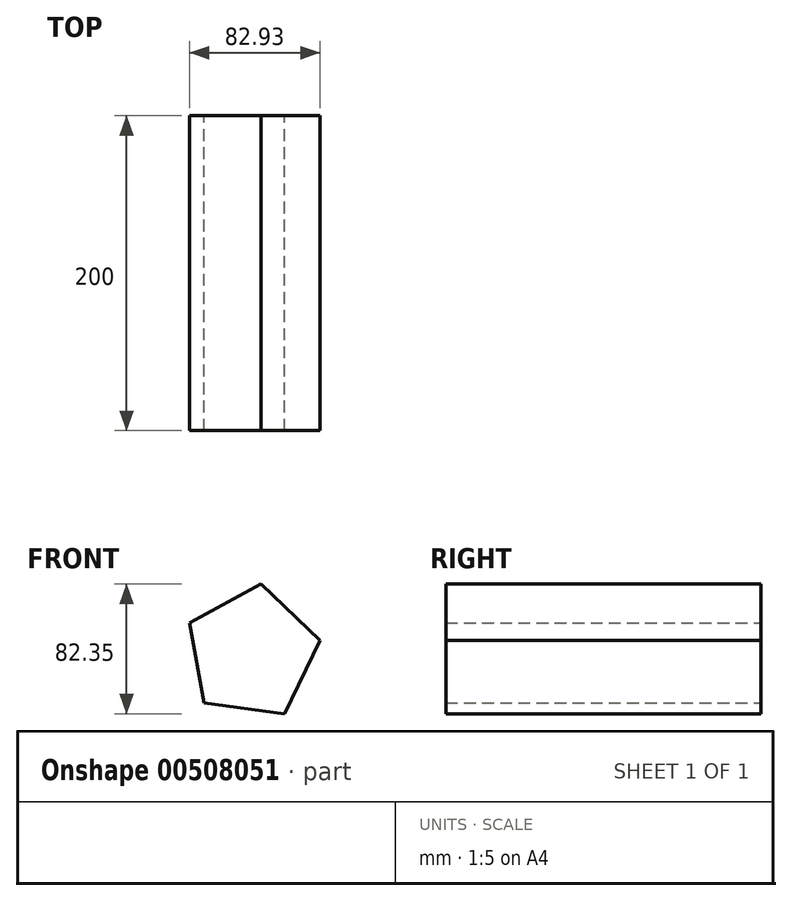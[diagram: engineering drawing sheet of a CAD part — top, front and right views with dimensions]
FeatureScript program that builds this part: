
annotation { "Feature Type Name" : "Feature", "Feature Type Description" : "" }
export const myFeature = defineFeature(function(context is Context, id is Id, definition is map)
    precondition{}
    {
        {
            var Q0;
            Q0=qCreatedBy(makeId("Front.planeOp"),FACE);
            var sketch = newSketch(context, id + "F0", { "sketchPlane" : qUnion([Q0])});
            skCircle(sketch, "E0.cCircle", {"center": v(0, 0) * mm, "radius": 44 * mm, "construction": true});
            skLineSegment(sketch, "E0.0", {"start": v(-39.64, 19.1) * mm, "end": v(5.9, 43.6) * mm});
            skLineSegment(sketch, "E0.1", {"start": v(5.9, 43.6) * mm, "end": v(43.3, 7.85) * mm});
            skLineSegment(sketch, "E0.2", {"start": v(43.3, 7.85) * mm, "end": v(20.85, -38.75) * mm});
            skLineSegment(sketch, "E0.3", {"start": v(20.85, -38.75) * mm, "end": v(-30.4, -31.8) * mm});
            skLineSegment(sketch, "E0.4", {"start": v(-30.4, -31.8) * mm, "end": v(-39.64, 19.1) * mm});
            skSolve(sketch);
        }
        {
            var Q0;
            Q0=makeQuery(id+"F0.imprint","IMPRINT",FACE,{"disambiguationData":[TD([[makeQuery(id+"F0.imprint","IMPRINT",EDGE,{"derivedFrom":sQuery(id+"F0.wireOp",EDGE,"E0.0")}),-1.0]])]});
            extrude(context, id + "F1", {"entities" : qUnion([Q0]), "endBound" : BoundingType.SYMMETRIC, "depth" : 200 * mm});
        }
    });
